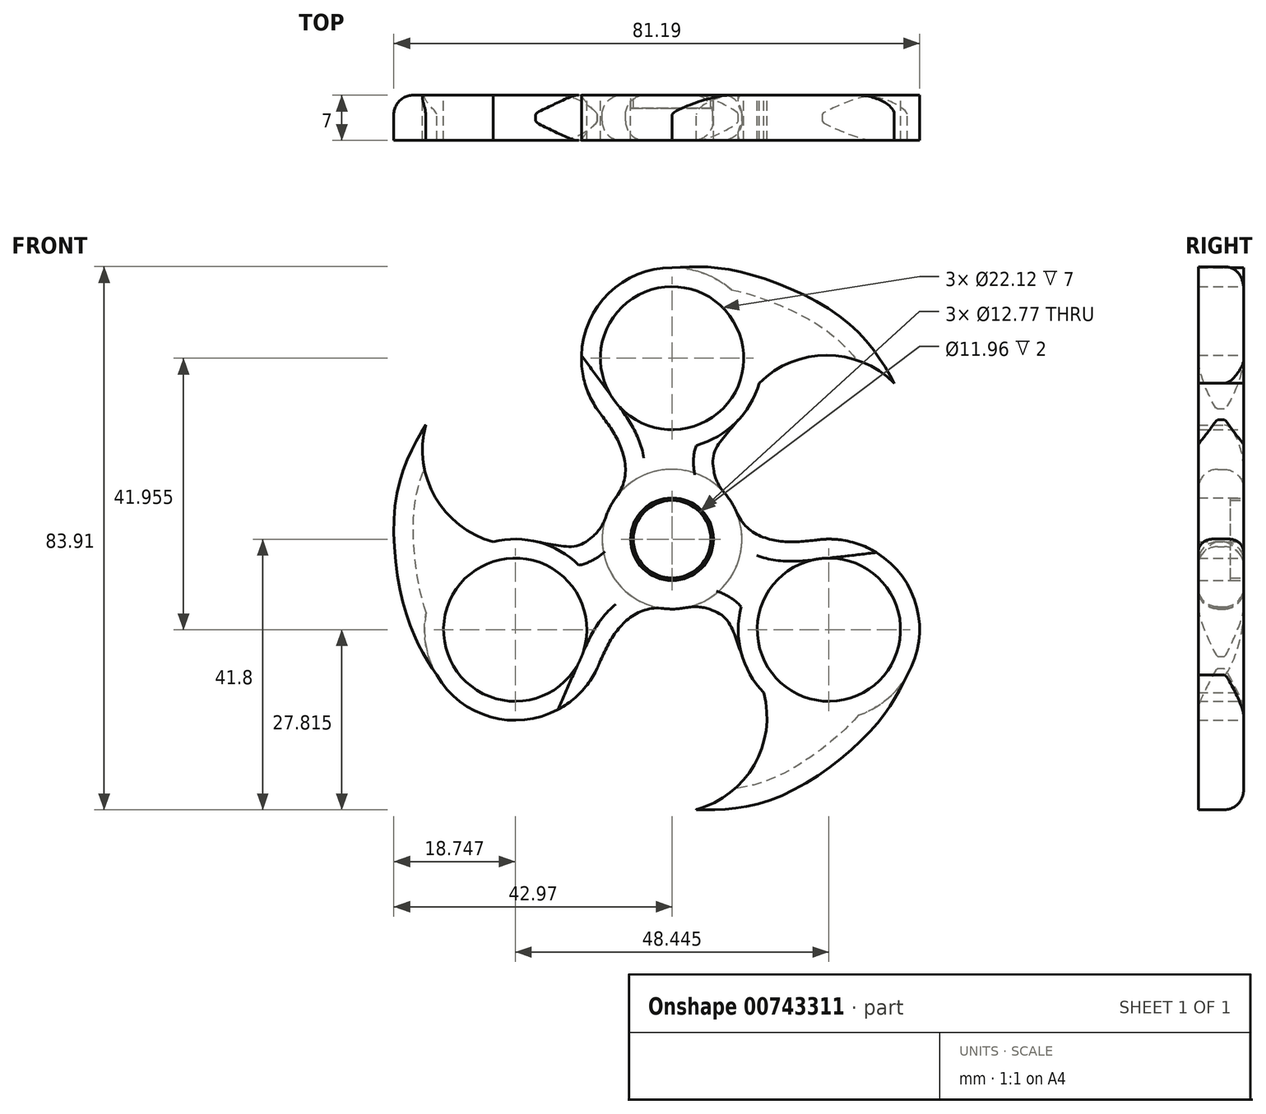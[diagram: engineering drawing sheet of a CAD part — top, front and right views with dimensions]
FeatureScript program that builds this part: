
annotation { "Feature Type Name" : "Feature", "Feature Type Description" : "" }
export const myFeature = defineFeature(function(context is Context, id is Id, definition is map)
    precondition{}
    {
        {
            var Q0;
            Q0=qCreatedBy(makeId("Front.planeOp"),FACE);
            var sketch = newSketch(context, id + "F0", { "sketchPlane" : qUnion([Q0])});
            skCircle(sketch, "E0", {"center": v(0, 0) * mm, "radius": 10.8 * mm});
            skCircle(sketch, "E1", {"center": v(0, 0) * mm, "radius": 6.35 * mm});
            skCircle(sketch, "E2", {"center": v(0, 27.97) * mm, "radius": 11.06 * mm});
            skCircle(sketch, "E3", {"center": v(0, 27.97) * mm, "radius": 14 * mm});
            skFitSpline(sketch, "E4", {"points": [v(-6.92, 8.28) * mm, v(-7.86, 14.1) * mm, v(-11.56, 20.08) * mm], "startDerivative": vector(-0.75, 12.33) * mm, "endDerivative": vector(-8.4, 11.28) * mm});
            skFitSpline(sketch, "E5", {"points": [v(7.19, 8.05) * mm, v(6.37, 12.74) * mm, v(10.25, 18.43) * mm], "startDerivative": vector(-4.56, 11.26) * mm, "endDerivative": vector(14.37, 16.76) * mm});
            skFitSpline(sketch, "E6", {"points": [v(0, 41.97) * mm, v(9.72, 41.5) * mm, v(26.98, 33.6) * mm, v(34.31, 24.12) * mm], "startDerivative": vector(29.37, 1.8) * mm, "endDerivative": vector(14.79, -27.24) * mm});
            skArc(sketch, "E7", {"start": v(34.31, 24.12) * mm, "mid": v(23.89, 28.42) * mm, "end": v(13.46, 24.12) * mm});
            skCircle(sketch, "E8", {"center": v(0, 0) * mm, "radius": 5.4 * mm});
            skCircle(sketch, "E9", {"center": v(0, 0) * mm, "radius": 6.38 * mm});
            skSolve(sketch);
        }
        {
            var Q0;
            {var subQ0=sQuery(id+"F0.wireOp",EDGE,"E6");Q0=makeQuery(id+"F0.imprint","IMPRINT",FACE,{"disambiguationData":[TD([[makeQuery(id+"F0.imprint","IMPRINT",EDGE,{"derivedFrom":subQ0}),-1.0]])]});}
            var Q1;
            Q1=makeQuery(id+"F0.imprint","IMPRINT",FACE,{"disambiguationData":[TD([[makeQuery(id+"F0.imprint","IMPRINT",EDGE,{"derivedFrom":sQuery(id+"F0.wireOp",EDGE,"E2")}),-1.0]])]});
            var Q2;
            {var subQ3=sQuery(id+"F0.wireOp",EDGE,"E5");Q2=makeQuery(id+"F0.imprint","IMPRINT",FACE,{"disambiguationData":[TD([[makeQuery(id+"F0.imprint","IMPRINT",EDGE,{"derivedFrom":subQ3}),1.0]])]});}
            var Q3;
            Q3=makeQuery(id+"F0.imprint","IMPRINT",FACE,{"disambiguationData":[TD([[makeQuery(id+"F0.imprint","IMPRINT",EDGE,{"derivedFrom":sQuery(id+"F0.wireOp",EDGE,"E9")}),-1.0]])]});
            extrude(context, id + "F1", {"entities" : qUnion([Q0, Q1, Q2, Q3]), "depth" : 7 * mm, "offsetDistance" : 25.4 * mm});
        }
        {
            var Q0;
            Q0=makeQuery(id+"F1.opExtrude","SWEPT_BODY",BODY,{"disambiguationData":[OSD([sQuery(id+"F0.wireOp",EDGE,"E0"),sQuery(id+"F0.wireOp",EDGE,"E1"),sQuery(id+"F0.wireOp",EDGE,"E2"),sQuery(id+"F0.wireOp",EDGE,"E3"),sQuery(id+"F0.wireOp",EDGE,"E4"),sQuery(id+"F0.wireOp",EDGE,"E5"),sQuery(id+"F0.wireOp",EDGE,"E6"),sQuery(id+"F0.wireOp",EDGE,"E7")])]});
            var Q1;
            Q1=makeQuery(id+"F1.opExtrude","CAP_EDGE",EDGE,{"disambiguationData":[OSD([sQuery(id+"F0.wireOp",EDGE,"E9")])],"isStart":false});
            circularPattern(context, id + "F2", {"entities" : qUnion([Q0]), "axis" : qUnion([Q1]), "angle" : 360 * degree, "instanceCount" : 3, "equalSpace" : true});
        }
        {
            var Q0;
            Q0=makeQuery(id+"F2.opPattern","COPY",EDGE,{"derivedFrom":makeQuery(id+"F1.opExtrude","SWEPT_EDGE",EDGE,{"disambiguationData":[OSD([sQuery(id+"F0.wireOp",EDGE,"E0"),sQuery(id+"F0.wireOp",EDGE,"E5")])]}),"instanceName":"1"});
            var Q1;
            Q1=makeQuery(id+"F1.opExtrude","SWEPT_EDGE",EDGE,{"disambiguationData":[OSD([sQuery(id+"F0.wireOp",EDGE,"E0"),sQuery(id+"F0.wireOp",EDGE,"E4")])]});
            var Q2;
            Q2=makeQuery(id+"F1.opExtrude","SWEPT_EDGE",EDGE,{"disambiguationData":[OSD([sQuery(id+"F0.wireOp",EDGE,"E0"),sQuery(id+"F0.wireOp",EDGE,"E5")])]});
            var Q3;
            Q3=makeQuery(id+"F2.opPattern","COPY",EDGE,{"derivedFrom":makeQuery(id+"F1.opExtrude","SWEPT_EDGE",EDGE,{"disambiguationData":[OSD([sQuery(id+"F0.wireOp",EDGE,"E0"),sQuery(id+"F0.wireOp",EDGE,"E4")])]}),"instanceName":"2"});
            var Q4;
            Q4=makeQuery(id+"F2.opPattern","COPY",EDGE,{"derivedFrom":makeQuery(id+"F1.opExtrude","SWEPT_EDGE",EDGE,{"disambiguationData":[OSD([sQuery(id+"F0.wireOp",EDGE,"E0"),sQuery(id+"F0.wireOp",EDGE,"E4")])]}),"instanceName":"1"});
            var Q5;
            Q5=makeQuery(id+"F2.opPattern","COPY",EDGE,{"derivedFrom":makeQuery(id+"F1.opExtrude","SWEPT_EDGE",EDGE,{"disambiguationData":[OSD([sQuery(id+"F0.wireOp",EDGE,"E0"),sQuery(id+"F0.wireOp",EDGE,"E5")])]}),"instanceName":"2"});
            fillet(context, id + "F3", {"entities" : qUnion([Q0, Q1, Q2, Q3, Q4, Q5]), "radius" : 7 * mm, "tangentPropagation" : true, "allowEdgeOverflow" : false});
        }
        {
            var Q0;
            Q0=makeQuery(id+"F1.opExtrude","CAP_EDGE",EDGE,{"disambiguationData":[OSD([sQuery(id+"F0.wireOp",EDGE,"E4")])],"isStart":false});
            var Q1;
            {var subQ0=sQuery(id+"F0.wireOp",EDGE,"E3");Q1=makeQuery(id+"F1.opExtrude","CAP_EDGE",EDGE,{"disambiguationData":[OSD([subQ0]),TDD([makeQuery(id+"F0.imprint","IMPRINT",EDGE,{"disambiguationData":[TD([[makeQuery(id+"F0.imprint","INTERSECT",VERTEX,{"disambiguationData":[OD(0.0)],"derivedFrom":[subQ0,sQuery(id+"F0.wireOp",EDGE,"E4")]}),1.0]])],"derivedFrom":subQ0})])],"isStart":false});}
            var Q2;
            {var subQ0=sQuery(id+"F0.wireOp",EDGE,"E3");Q2=makeQuery(id+"F2.opPattern","COPY",EDGE,{"derivedFrom":makeQuery(id+"F1.opExtrude","CAP_EDGE",EDGE,{"disambiguationData":[OSD([subQ0]),TDD([makeQuery(id+"F0.imprint","IMPRINT",EDGE,{"disambiguationData":[TD([[makeQuery(id+"F0.imprint","INTERSECT",VERTEX,{"disambiguationData":[OD(0.0)],"derivedFrom":[subQ0,sQuery(id+"F0.wireOp",EDGE,"E4")]}),1.0]])],"derivedFrom":subQ0})])],"isStart":false}),"instanceName":"2"});}
            var Q3;
            Q3=makeQuery(id+"F2.opPattern","COPY",EDGE,{"derivedFrom":makeQuery(id+"F1.opExtrude","CAP_EDGE",EDGE,{"disambiguationData":[OSD([sQuery(id+"F0.wireOp",EDGE,"E4")])],"isStart":false}),"instanceName":"2"});
            var Q4;
            Q4=makeQuery(id+"F2.opPattern","COPY",EDGE,{"derivedFrom":makeQuery(id+"F1.opExtrude","CAP_EDGE",EDGE,{"disambiguationData":[OSD([sQuery(id+"F0.wireOp",EDGE,"E4")])],"isStart":false}),"instanceName":"1"});
            var Q5;
            {var subQ0=sQuery(id+"F0.wireOp",EDGE,"E3");Q5=makeQuery(id+"F2.opPattern","COPY",EDGE,{"derivedFrom":makeQuery(id+"F1.opExtrude","CAP_EDGE",EDGE,{"disambiguationData":[OSD([subQ0]),TDD([makeQuery(id+"F0.imprint","IMPRINT",EDGE,{"disambiguationData":[TD([[makeQuery(id+"F0.imprint","INTERSECT",VERTEX,{"disambiguationData":[OD(0.0)],"derivedFrom":[subQ0,sQuery(id+"F0.wireOp",EDGE,"E4")]}),1.0]])],"derivedFrom":subQ0})])],"isStart":false}),"instanceName":"1"});}
            var Q6;
            Q6=makeQuery(id+"F2.opPattern","COPY",EDGE,{"derivedFrom":makeQuery(id+"F1.opExtrude","CAP_EDGE",EDGE,{"disambiguationData":[OSD([sQuery(id+"F0.wireOp",EDGE,"E6")])],"isStart":true}),"instanceName":"1"});
            var Q7;
            Q7=makeQuery(id+"F2.opPattern","COPY",EDGE,{"derivedFrom":makeQuery(id+"F1.opExtrude","CAP_EDGE",EDGE,{"disambiguationData":[OSD([sQuery(id+"F0.wireOp",EDGE,"E6")])],"isStart":true}),"instanceName":"2"});
            var Q8;
            Q8=makeQuery(id+"F1.opExtrude","CAP_EDGE",EDGE,{"disambiguationData":[OSD([sQuery(id+"F0.wireOp",EDGE,"E6")])],"isStart":true});
            var Q9;
            {var subQ0=sQuery(id+"F0.wireOp",EDGE,"E3");Q9=makeQuery(id+"F1.opExtrude","CAP_EDGE",EDGE,{"disambiguationData":[OSD([subQ0]),TDD([makeQuery(id+"F0.imprint","IMPRINT",EDGE,{"disambiguationData":[TD([[makeQuery(id+"F0.imprint","INTERSECT",VERTEX,{"disambiguationData":[OD(0.0)],"derivedFrom":[subQ0,sQuery(id+"F0.wireOp",EDGE,"E4")]}),1.0]])],"derivedFrom":subQ0})])],"isStart":true});}
            var Q10;
            Q10=makeQuery(id+"F1.opExtrude","CAP_EDGE",EDGE,{"disambiguationData":[OSD([sQuery(id+"F0.wireOp",EDGE,"E4")])],"isStart":true});
            var Q11;
            Q11=makeQuery(id+"F2.opPattern","COPY",EDGE,{"derivedFrom":makeQuery(id+"F1.opExtrude","CAP_EDGE",EDGE,{"disambiguationData":[OSD([sQuery(id+"F0.wireOp",EDGE,"E4")])],"isStart":true}),"instanceName":"2"});
            var Q12;
            {var subQ0=sQuery(id+"F0.wireOp",EDGE,"E3");Q12=makeQuery(id+"F2.opPattern","COPY",EDGE,{"derivedFrom":makeQuery(id+"F1.opExtrude","CAP_EDGE",EDGE,{"disambiguationData":[OSD([subQ0]),TDD([makeQuery(id+"F0.imprint","IMPRINT",EDGE,{"disambiguationData":[TD([[makeQuery(id+"F0.imprint","INTERSECT",VERTEX,{"disambiguationData":[OD(0.0)],"derivedFrom":[subQ0,sQuery(id+"F0.wireOp",EDGE,"E4")]}),1.0]])],"derivedFrom":subQ0})])],"isStart":true}),"instanceName":"1"});}
            var Q13;
            Q13=makeQuery(id+"F2.opPattern","COPY",EDGE,{"derivedFrom":makeQuery(id+"F1.opExtrude","CAP_EDGE",EDGE,{"disambiguationData":[OSD([sQuery(id+"F0.wireOp",EDGE,"E4")])],"isStart":true}),"instanceName":"1"});
            fillet(context, id + "F4", {"entities" : qUnion([Q0, Q1, Q2, Q3, Q4, Q5, Q6, Q7, Q8, Q9, Q10, Q11, Q12, Q13]), "radius" : 3 * mm, "tangentPropagation" : true, "allowEdgeOverflow" : false});
        }
        {
            var Q0;
            Q0=makeQuery(id+"F1.opExtrude","CAP_FACE",FACE,{"disambiguationData":[OSD([sQuery(id+"F0.wireOp",EDGE,"E0"),sQuery(id+"F0.wireOp",EDGE,"E1"),sQuery(id+"F0.wireOp",EDGE,"E2"),sQuery(id+"F0.wireOp",EDGE,"E3"),sQuery(id+"F0.wireOp",EDGE,"E4"),sQuery(id+"F0.wireOp",EDGE,"E5"),sQuery(id+"F0.wireOp",EDGE,"E6"),sQuery(id+"F0.wireOp",EDGE,"E7")])],"isStart":false});
            var sketch = newSketch(context, id + "F5", { "sketchPlane" : qUnion([Q0])});
            skLineSegment(sketch, "E10.bottom", {"start": v(-3.12, 16.14) * mm, "end": v(3.09, 16.14) * mm});
            skLineSegment(sketch, "E10.top", {"start": v(-3.12, 14.7) * mm, "end": v(3.09, 14.7) * mm});
            skLineSegment(sketch, "E10.left", {"start": v(-3.12, 16.14) * mm, "end": v(-3.12, 14.7) * mm});
            skLineSegment(sketch, "E10.right", {"start": v(3.09, 16.14) * mm, "end": v(3.09, 14.7) * mm});
            skLineSegment(sketch, "E11.bottom", {"start": v(1.12, 14.7) * mm, "end": v(-0.23, 14.7) * mm});
            skLineSegment(sketch, "E11.top", {"start": v(1.12, 9.07) * mm, "end": v(-0.23, 9.07) * mm});
            skLineSegment(sketch, "E11.left", {"start": v(1.12, 14.7) * mm, "end": v(1.12, 9.07) * mm});
            skLineSegment(sketch, "E11.right", {"start": v(-0.23, 14.7) * mm, "end": v(-0.23, 9.07) * mm});
            skArc(sketch, "E12", {"start": v(-4.33, 9.07) * mm, "mid": v(-1.6, 7.98) * mm, "end": v(1.12, 9.07) * mm});
            skArc(sketch, "E13", {"start": v(-3.85, 10.06) * mm, "mid": v(-2.07, 9.12) * mm, "end": v(-0.23, 9.9) * mm});
            skLineSegment(sketch, "E14", {"start": v(-4.33, 9.07) * mm, "end": v(-3.85, 10.06) * mm});
            skSolve(sketch);
        }
        {
            var Q0;
            {var subQ6=sQuery(id+"F5.wireOp",EDGE,"E11.top");Q0=makeQuery(id+"F5.imprint","IMPRINT",FACE,{"disambiguationData":[TD([[makeQuery(id+"F5.imprint","IMPRINT",EDGE,{"derivedFrom":subQ6}),-1.0]])]});}
            var Q1;
            {var subQ6=sQuery(id+"F5.wireOp",EDGE,"E10.bottom");Q1=makeQuery(id+"F5.imprint","IMPRINT",FACE,{"disambiguationData":[TD([[makeQuery(id+"F5.imprint","IMPRINT",EDGE,{"derivedFrom":subQ6}),-1.0]])]});}
            var Q2;
            {var subQ2=sQuery(id+"F5.wireOp",EDGE,"E11.top");Q2=makeQuery(id+"F5.imprint","IMPRINT",FACE,{"disambiguationData":[TD([[makeQuery(id+"F5.imprint","IMPRINT",EDGE,{"derivedFrom":subQ2}),1.0]])]});}
            extrude(context, id + "F6", {"entities" : qUnion([Q0, Q1, Q2]), "depth" : 2 * mm, "offsetDistance" : 25.4 * mm});
        }
        {
            var Q0;
            Q0=makeQuery(id+"F6.opExtrude","SWEPT_EDGE",EDGE,{"disambiguationData":[OSD([sQuery(id+"F5.wireOp",EDGE,"E11.top"),sQuery(id+"F5.wireOp",EDGE,"E11.left"),sQuery(id+"F5.wireOp",EDGE,"E12")])]});
            var Q1;
            Q1=makeQuery(id+"F6.opExtrude","SWEPT_EDGE",EDGE,{"disambiguationData":[OSD([sQuery(id+"F5.wireOp",EDGE,"E11.right"),sQuery(id+"F5.wireOp",EDGE,"E13")])]});
            chamfer(context, id + "F7", {"entities" : qUnion([Q0, Q1]), "width" : .5 * mm, "tangentPropagation" : true});
        }
        {
            var Q0;
            Q0=makeQuery(id+"F6.opExtrude","SWEPT_EDGE",EDGE,{"disambiguationData":[OSD([sQuery(id+"F5.wireOp",EDGE,"E10.top"),sQuery(id+"F5.wireOp",EDGE,"E11.bottom"),sQuery(id+"F5.wireOp",EDGE,"E11.left")])]});
            var Q1;
            Q1=makeQuery(id+"F6.opExtrude","SWEPT_EDGE",EDGE,{"disambiguationData":[OSD([sQuery(id+"F5.wireOp",EDGE,"E10.top"),sQuery(id+"F5.wireOp",EDGE,"E11.bottom"),sQuery(id+"F5.wireOp",EDGE,"E11.right")])]});
            var Q2;
            Q2=makeQuery(id+"F6.opExtrude","SWEPT_EDGE",EDGE,{"disambiguationData":[OSD([sQuery(id+"F5.wireOp",EDGE,"E10.top"),sQuery(id+"F5.wireOp",EDGE,"E10.left")])]});
            var Q3;
            Q3=makeQuery(id+"F6.opExtrude","SWEPT_EDGE",EDGE,{"disambiguationData":[OSD([sQuery(id+"F5.wireOp",EDGE,"E10.bottom"),sQuery(id+"F5.wireOp",EDGE,"E10.left")])]});
            var Q4;
            Q4=makeQuery(id+"F6.opExtrude","SWEPT_EDGE",EDGE,{"disambiguationData":[OSD([sQuery(id+"F5.wireOp",EDGE,"E10.bottom"),sQuery(id+"F5.wireOp",EDGE,"E10.right")])]});
            var Q5;
            Q5=makeQuery(id+"F6.opExtrude","SWEPT_EDGE",EDGE,{"disambiguationData":[OSD([sQuery(id+"F5.wireOp",EDGE,"E10.top"),sQuery(id+"F5.wireOp",EDGE,"E10.right")])]});
            var Q6;
            Q6=makeQuery(id+"F6.opExtrude","SWEPT_EDGE",EDGE,{"disambiguationData":[OSD([sQuery(id+"F5.wireOp",EDGE,"E13"),sQuery(id+"F5.wireOp",EDGE,"E14")])]});
            var Q7;
            Q7=makeQuery(id+"F6.opExtrude","SWEPT_EDGE",EDGE,{"disambiguationData":[OSD([sQuery(id+"F0.wireOp",EDGE,"E0"),sQuery(id+"F0.wireOp",EDGE,"E1"),sQuery(id+"F0.wireOp",EDGE,"E2"),sQuery(id+"F0.wireOp",EDGE,"E3"),sQuery(id+"F0.wireOp",EDGE,"E4"),sQuery(id+"F0.wireOp",EDGE,"E5"),sQuery(id+"F0.wireOp",EDGE,"E6"),sQuery(id+"F0.wireOp",EDGE,"E7"),sQuery(id+"F5.wireOp",EDGE,"E12"),sQuery(id+"F5.wireOp",EDGE,"E14")])]});
            fillet(context, id + "F8", {"entities" : qUnion([Q0, Q1, Q2, Q3, Q4, Q5, Q6, Q7]), "radius" : .5 * mm, "tangentPropagation" : true, "allowEdgeOverflow" : false});
        }
        {
            var Q0;
            Q0=makeQuery(id+"F6.opExtrude","SWEPT_BODY",BODY,{"disambiguationData":[OSD([sQuery(id+"F5.wireOp",EDGE,"E10.bottom"),sQuery(id+"F5.wireOp",EDGE,"E10.top"),sQuery(id+"F5.wireOp",EDGE,"E10.left"),sQuery(id+"F5.wireOp",EDGE,"E10.right"),sQuery(id+"F5.wireOp",EDGE,"E11.left"),sQuery(id+"F5.wireOp",EDGE,"E11.right"),sQuery(id+"F5.wireOp",EDGE,"E12"),sQuery(id+"F5.wireOp",EDGE,"E13"),sQuery(id+"F5.wireOp",EDGE,"E14")])]});
            var Q1;
            Q1=makeQuery(id+"F1.opExtrude","SWEPT_FACE",FACE,{"disambiguationData":[OSD([sQuery(id+"F0.wireOp",EDGE,"E9")])]});
            circularPattern(context, id + "F9", {"entities" : qUnion([Q0]), "axis" : qUnion([Q1]), "angle" : 360 * degree, "instanceCount" : 3, "equalSpace" : true});
        }
        {
            var Q0;
            Q0=qCreatedBy(makeId("Front.planeOp"),FACE);
            var sketch = newSketch(context, id + "F10", { "sketchPlane" : qUnion([Q0])});
            skCircle(sketch, "E15", {"center": v(0, 0) * mm, "radius": 5.98 * mm});
            skCircle(sketch, "E16", {"center": v(0, 0) * mm, "radius": 6.35 * mm});
            skSolve(sketch);
        }
        {
            var Q0;
            Q0=makeQuery(id+"F10.imprint","IMPRINT",FACE,{"disambiguationData":[TD([[makeQuery(id+"F10.imprint","IMPRINT",EDGE,{"derivedFrom":sQuery(id+"F10.wireOp",EDGE,"E15")}),-1.0]])]});
            extrude(context, id + "F11", {"entities" : qUnion([Q0]), "depth" : 2 * mm, "offsetDistance" : 25.4 * mm});
        }
        {
            var Q0;
            Q0=makeQuery(id+"F6.opExtrude","SWEPT_BODY",BODY,{"disambiguationData":[OSD([sQuery(id+"F5.wireOp",EDGE,"E10.bottom"),sQuery(id+"F5.wireOp",EDGE,"E10.top"),sQuery(id+"F5.wireOp",EDGE,"E10.left"),sQuery(id+"F5.wireOp",EDGE,"E10.right"),sQuery(id+"F5.wireOp",EDGE,"E11.left"),sQuery(id+"F5.wireOp",EDGE,"E11.right"),sQuery(id+"F5.wireOp",EDGE,"E12"),sQuery(id+"F5.wireOp",EDGE,"E13"),sQuery(id+"F5.wireOp",EDGE,"E14")])]});
            deleteBodies(context, id + "F12", {"entities" : qUnion([Q0])});
        }
        {
            var Q0;
            Q0=makeQuery(id+"F9.opPattern","COPY",BODY,{"derivedFrom":makeQuery(id+"F6.opExtrude","SWEPT_BODY",BODY,{"disambiguationData":[OSD([sQuery(id+"F5.wireOp",EDGE,"E10.bottom"),sQuery(id+"F5.wireOp",EDGE,"E10.top"),sQuery(id+"F5.wireOp",EDGE,"E10.left"),sQuery(id+"F5.wireOp",EDGE,"E10.right"),sQuery(id+"F5.wireOp",EDGE,"E11.left"),sQuery(id+"F5.wireOp",EDGE,"E11.right"),sQuery(id+"F5.wireOp",EDGE,"E12"),sQuery(id+"F5.wireOp",EDGE,"E13"),sQuery(id+"F5.wireOp",EDGE,"E14")])]}),"instanceName":"2"});
            deleteBodies(context, id + "F13", {"entities" : qUnion([Q0])});
        }
        {
            var Q0;
            Q0=makeQuery(id+"F9.opPattern","COPY",BODY,{"derivedFrom":makeQuery(id+"F6.opExtrude","SWEPT_BODY",BODY,{"disambiguationData":[OSD([sQuery(id+"F5.wireOp",EDGE,"E10.bottom"),sQuery(id+"F5.wireOp",EDGE,"E10.top"),sQuery(id+"F5.wireOp",EDGE,"E10.left"),sQuery(id+"F5.wireOp",EDGE,"E10.right"),sQuery(id+"F5.wireOp",EDGE,"E11.left"),sQuery(id+"F5.wireOp",EDGE,"E11.right"),sQuery(id+"F5.wireOp",EDGE,"E12"),sQuery(id+"F5.wireOp",EDGE,"E13"),sQuery(id+"F5.wireOp",EDGE,"E14")])]}),"instanceName":"1"});
            deleteBodies(context, id + "F14", {"entities" : qUnion([Q0])});
        }
    });
